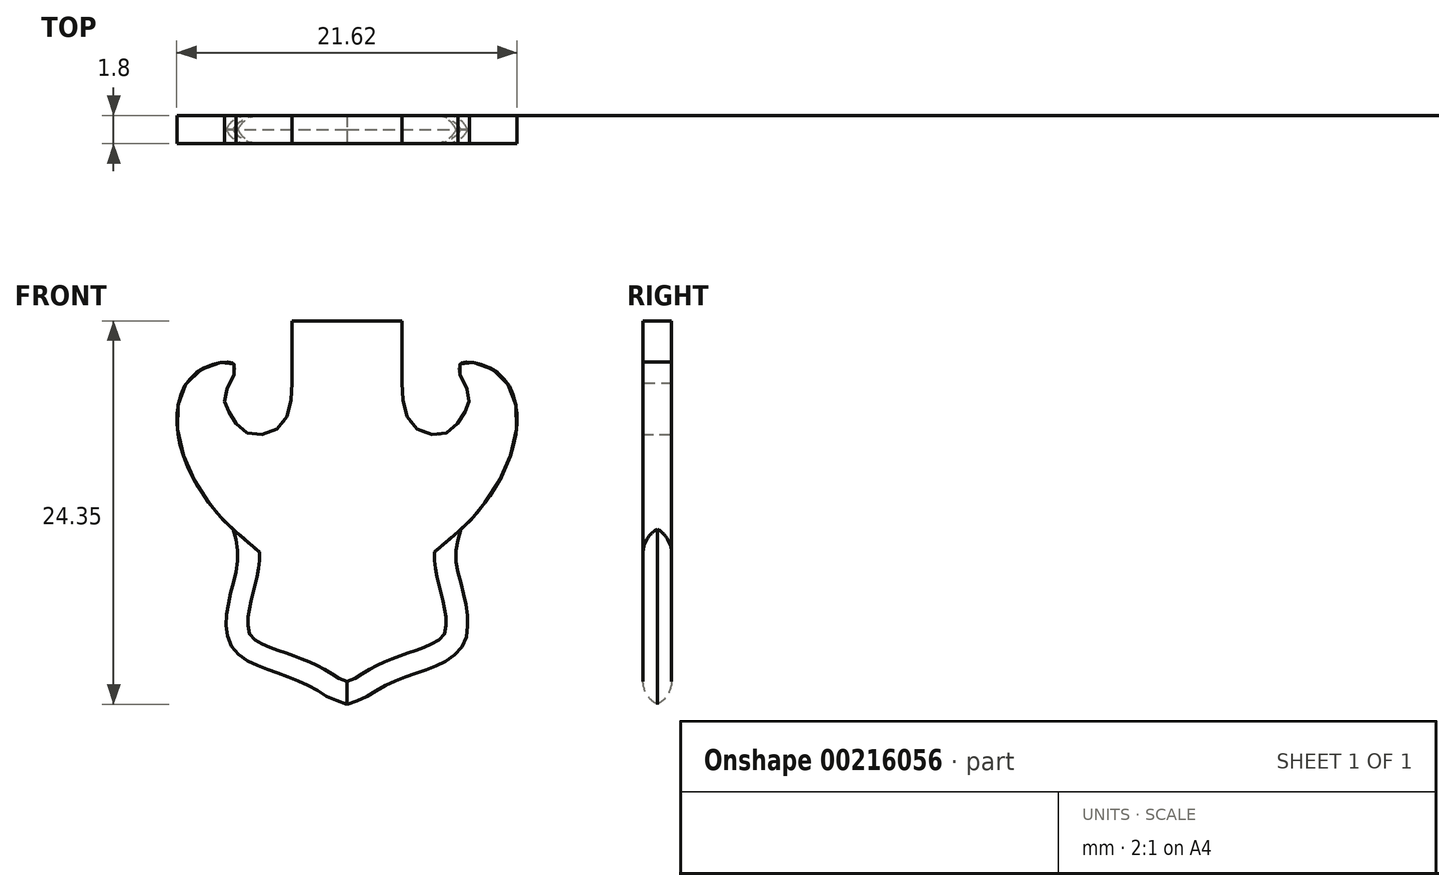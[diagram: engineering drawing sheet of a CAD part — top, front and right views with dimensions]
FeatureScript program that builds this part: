
annotation { "Feature Type Name" : "Feature", "Feature Type Description" : "" }
export const myFeature = defineFeature(function(context is Context, id is Id, definition is map)
    precondition{}
    {
        {
            var Q0;
            Q0=qCreatedBy(makeId("Front.planeOp"),FACE);
            var sketch = newSketch(context, id + "F0", { "sketchPlane" : qUnion([Q0])});
            skLineSegment(sketch, "E0", {"start": v(3.5, 0) * mm, "end": v(3.5, 3.94) * mm});
            skLineSegment(sketch, "E1", {"start": v(3.5, 3.94) * mm, "end": v(0, 3.94) * mm});
            skFitSpline(sketch, "E2", {"points": [v(3.5, 0) * mm, v(4.1, -2.6) * mm, v(6.2, -3.22) * mm, v(7.5, -1.88) * mm, v(7.71, -0.66) * mm, v(7.1, 1.12) * mm, v(9.66, 0.57) * mm, v(10.5, -4.28) * mm, v(7.44, -9.13) * mm], "startDerivative": vector(0.4, -20.95) * mm, "endDerivative": vector(-15.61, -13.53) * mm});
            skFitSpline(sketch, "E3", {"points": [v(7.44, -9.13) * mm, v(7.38, -12.8) * mm, v(7.44, -16.81) * mm, v(3.7, -18.82) * mm, v(1.75, -19.76) * mm, v(0, -20.54) * mm], "startDerivative": vector(-8.74, -24.48) * mm, "endDerivative": vector(-24.79, -8.05) * mm});
            skLineSegment(sketch, "E4.MirrorCS", {"start": v(-3.5, 3.94) * mm, "end": v(0, 3.94) * mm});
            skFitSpline(sketch, "E5.MirrorCS", {"points": [v(-7.44, -9.13) * mm, v(-7.38, -12.8) * mm, v(-7.44, -16.81) * mm, v(-3.7, -18.82) * mm, v(-1.75, -19.76) * mm, v(0, -20.54) * mm], "startDerivative": vector(8.74, -24.48) * mm, "endDerivative": vector(24.79, -8.05) * mm});
            skFitSpline(sketch, "E6.MirrorCS", {"points": [v(-3.5, 0) * mm, v(-4.1, -2.6) * mm, v(-6.2, -3.22) * mm, v(-7.5, -1.88) * mm, v(-7.71, -0.66) * mm, v(-7.1, 1.12) * mm, v(-9.66, 0.57) * mm, v(-10.5, -4.28) * mm, v(-7.44, -9.13) * mm], "startDerivative": vector(-0.4, -20.95) * mm, "endDerivative": vector(15.61, -13.53) * mm});
            skLineSegment(sketch, "E7.MirrorCS", {"start": v(-3.5, 0) * mm, "end": v(-3.5, 3.94) * mm});
            skSolve(sketch);
        }
        {
            var Q0;
            Q0 = qSketchRegion(id + "F0", true);
            extrude(context, id + "F1", {"entities" : qUnion([Q0]), "depth" : 1.8 * mm});
        }
        {
            var Q0;
            Q0 = qSketchRegion(id + "F0", true);
            extrude(context, id + "F2", {"entities" : qUnion([Q0]), "operationType" : NewBodyOperationType.ADD, "depth" : 1.8 * mm});
        }
        {
            var Q0;
            Q0=makeQuery(id+"F1.opExtrude","CAP_EDGE",EDGE,{"disambiguationData":[OSD([sQuery(id+"F0.wireOp",EDGE,"E5.MirrorCS")])],"isStart":false});
            var Q1;
            Q1=makeQuery(id+"F1.opExtrude","CAP_EDGE",EDGE,{"disambiguationData":[OSD([sQuery(id+"F0.wireOp",EDGE,"E3")])],"isStart":false});
            fillet(context, id + "F3", {"entities" : qUnion([Q0, Q1]), "radius" : 1.5 * mm, "tangentPropagation" : true, "allowEdgeOverflow" : false});
        }
        {
            var Q0;
            Q0=makeQuery(id+"F1.opExtrude","CAP_EDGE",EDGE,{"disambiguationData":[OSD([sQuery(id+"F0.wireOp",EDGE,"E5.MirrorCS")])],"isStart":true});
            var Q1;
            Q1=makeQuery(id+"F1.opExtrude","CAP_EDGE",EDGE,{"disambiguationData":[OSD([sQuery(id+"F0.wireOp",EDGE,"E3")])],"isStart":true});
            fillet(context, id + "F4", {"entities" : qUnion([Q0, Q1]), "radius" : 1.5 * mm, "tangentPropagation" : true, "allowEdgeOverflow" : false});
        }
    });
